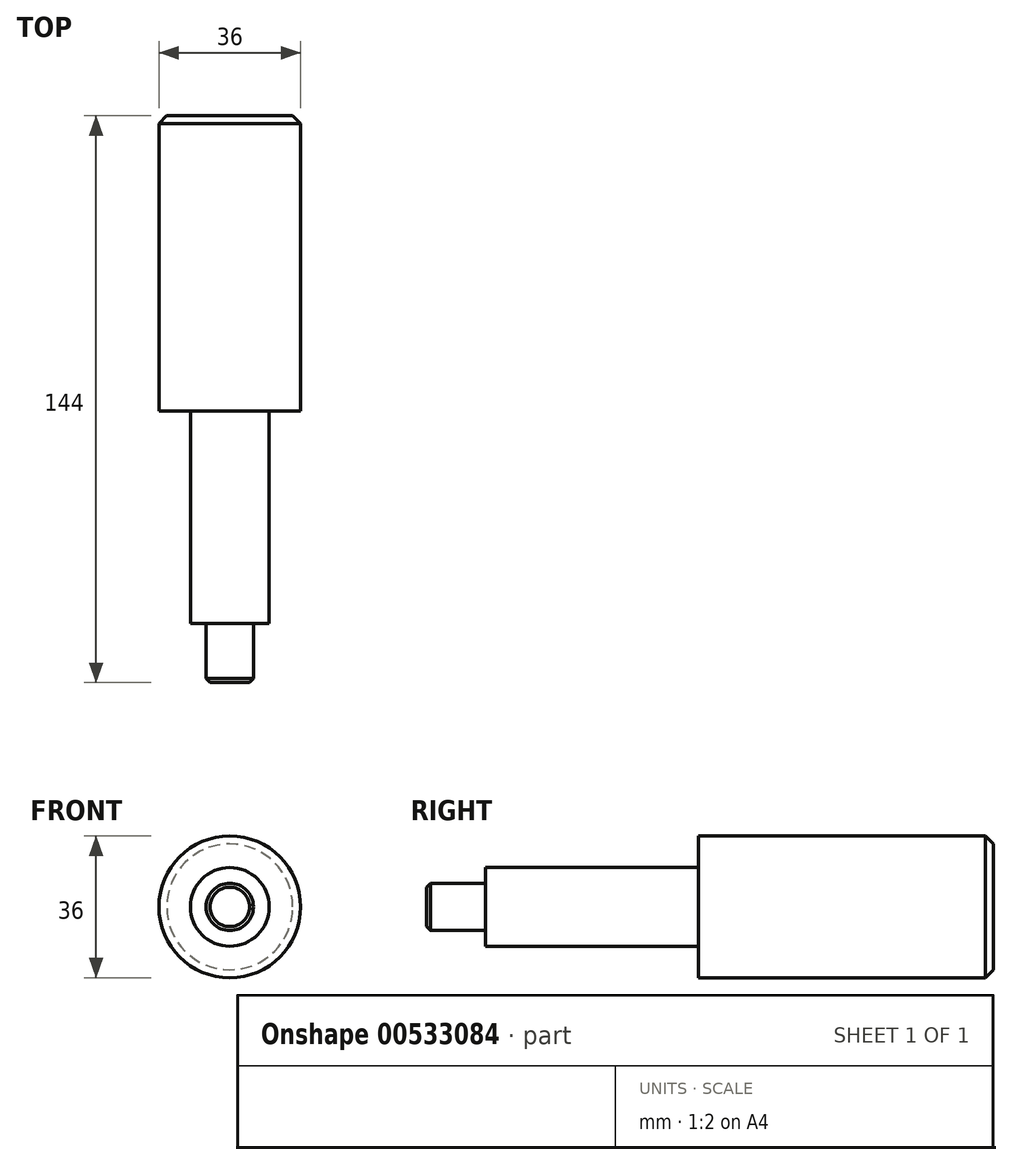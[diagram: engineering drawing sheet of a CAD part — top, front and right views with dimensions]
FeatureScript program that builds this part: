
annotation { "Feature Type Name" : "Feature", "Feature Type Description" : "" }
export const myFeature = defineFeature(function(context is Context, id is Id, definition is map)
    precondition{}
    {
        {
            var Q0;
            Q0=qCreatedBy(makeId("Front.planeOp"),FACE);
            var sketch = newSketch(context, id + "F0", { "sketchPlane" : qUnion([Q0])});
            skCircle(sketch, "E0", {"center": v(0, 0) * mm, "radius": 10 * mm});
            skSolve(sketch);
        }
        {
            var Q0;
            Q0 = qSketchRegion(id + "F0", true);
            extrude(context, id + "F1", {"entities" : qUnion([Q0]), "depth" : 54 * mm, "offsetDistance" : 25 * mm});
        }
        {
            var Q0;
            Q0=makeQuery(id+"F1.opExtrude","CAP_FACE",FACE,{"disambiguationData":[OSD([sQuery(id+"F0.wireOp",EDGE,"E0")])],"isStart":false});
            var sketch = newSketch(context, id + "F2", { "sketchPlane" : qUnion([Q0])});
            skCircle(sketch, "E1", {"center": v(0, 0) * mm, "radius": 6 * mm});
            skSolve(sketch);
        }
        {
            var Q0;
            Q0 = qSketchRegion(id + "F2", true);
            extrude(context, id + "F3", {"entities" : qUnion([Q0]), "operationType" : NewBodyOperationType.ADD, "depth" : 15 * mm, "offsetDistance" : 25 * mm});
        }
        {
            var Q0;
            Q0=makeQuery(id+"F1.opExtrude","CAP_FACE",FACE,{"disambiguationData":[OSD([sQuery(id+"F0.wireOp",EDGE,"E0")])],"isStart":true});
            var sketch = newSketch(context, id + "F4", { "sketchPlane" : qUnion([Q0])});
            skCircle(sketch, "E2", {"center": v(0, 0) * mm, "radius": 18 * mm});
            skSolve(sketch);
        }
        {
            var Q0;
            Q0 = qSketchRegion(id + "F4", true);
            extrude(context, id + "F5", {"entities" : qUnion([Q0]), "operationType" : NewBodyOperationType.ADD, "depth" : 75 * mm, "offsetDistance" : 25 * mm});
        }
        {
            var Q0;
            Q0=makeQuery(id+"F5.opExtrude","CAP_EDGE",EDGE,{"disambiguationData":[OSD([sQuery(id+"F4.wireOp",EDGE,"E2")])],"isStart":false});
            chamfer(context, id + "F6", {"entities" : qUnion([Q0]), "width" : 2 * mm, "tangentPropagation" : true});
        }
        {
            var Q0;
            Q0=makeQuery(id+"F3.opExtrude","CAP_EDGE",EDGE,{"disambiguationData":[OSD([sQuery(id+"F2.wireOp",EDGE,"E1")])],"isStart":false});
            chamfer(context, id + "F7", {"entities" : qUnion([Q0]), "width" : 1 * mm, "tangentPropagation" : true});
        }
    });
